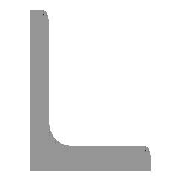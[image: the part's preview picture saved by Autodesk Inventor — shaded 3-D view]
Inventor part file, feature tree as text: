
AUTODESK INVENTOR PART (.ipt)
format: ipt  version: 2024.1 (Build 281209000, 209)  size: 120,320 bytes
history: native  units: mm (DEFAULTED — no unit token found)
features: other x4, sketch x1, plane x1
ambient origin geometry x8: Origin, YZ Plane, XZ Plane, XY Plane, X Axis, Y Axis, Z Axis, Center Point
bodies: Solid1 (feature_tree), Body (feature_tree)
feature tree (6):
  parser-record x1  (decoder bookkeeping rows leaked as tree rows — omitted from the tree; the rows remain in map.json)
  other  "Driven Length"
  other  "Start Plane"
  other  "End Plane"
  sketch  "Sketch3"  dims[d0=25.4mm d1=25.4mm d2=3.175mm d3=3.175mm d4=1300.0mm d5=0.0mm d10=0.0mm d11=0.0mm d12=-0.0mm d13=1300.0mm d14=3.302mm d15=1.524mm d16=90.0deg d17=1300.0mm]
  plane  "Work Plane3"
